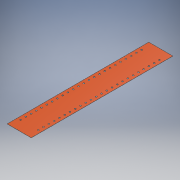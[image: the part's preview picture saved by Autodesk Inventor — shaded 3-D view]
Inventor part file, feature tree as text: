
AUTODESK INVENTOR PART (.ipt)
format: ipt  version: 2019 (Build 230136000, 136)  size: 206,848 bytes
history: native  units: mm
features: extrude x2, other x2, mirror x1
ambient origin geometry x8: Origin, YZ Plane, XZ Plane, XY Plane, X Axis, Y Axis, Z Axis, Center Point
bodies: Body1 (feature_tree)
feature tree (5):
  extrude  "Skin Body"  Depth=1095.0mm
  extrude  "End Cut"  Depth=547.5mm
  mirror  "End Cut Mirror"
  other  "Skin Scheme"
  other  "End Cut Outline"
